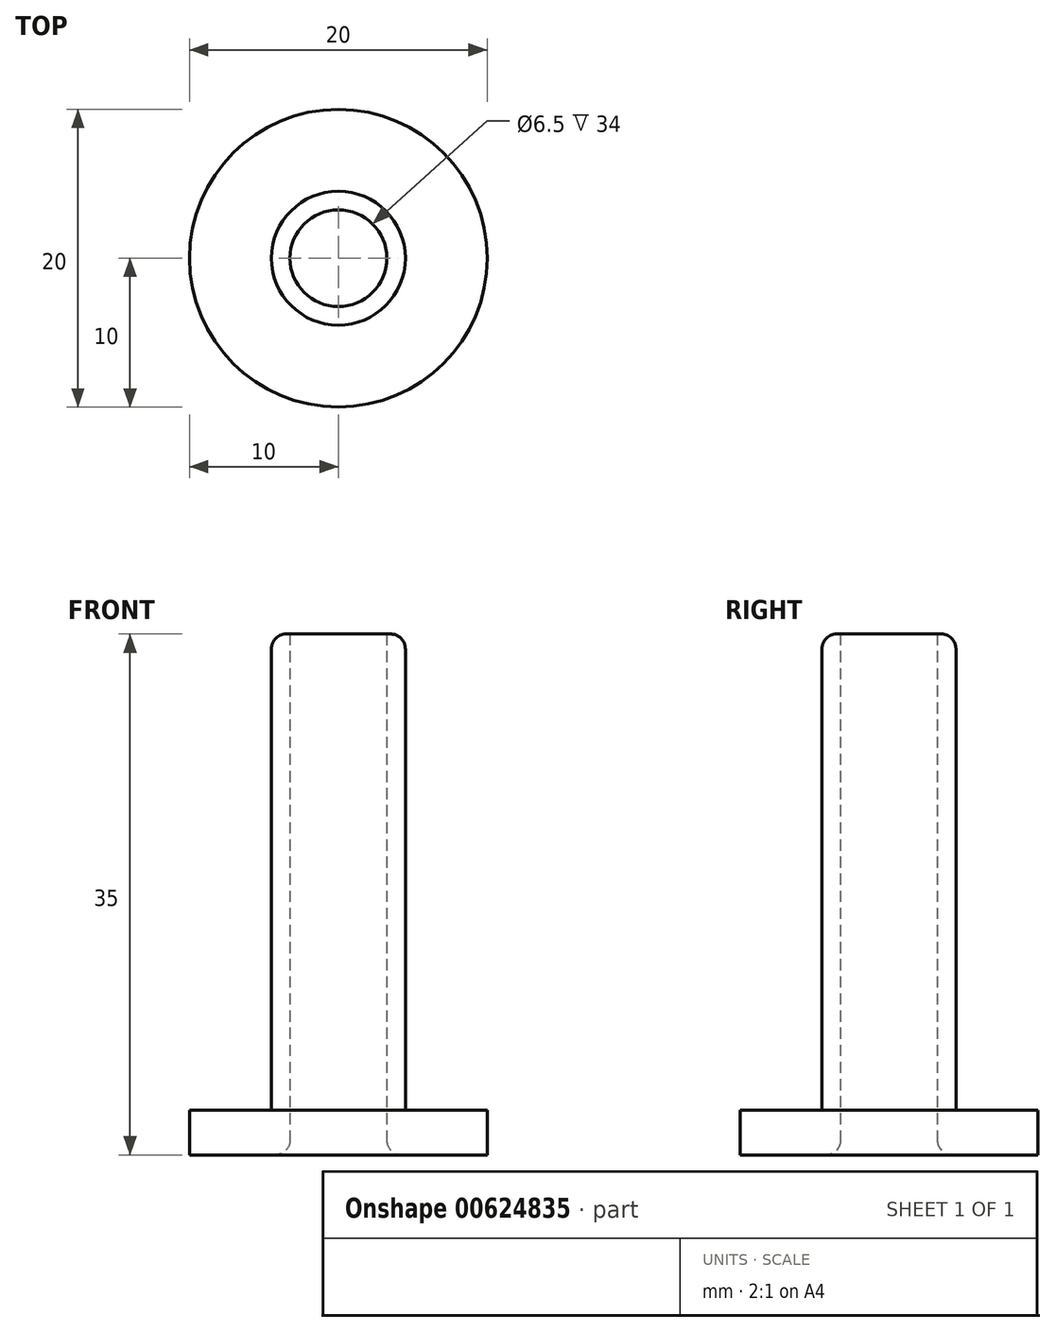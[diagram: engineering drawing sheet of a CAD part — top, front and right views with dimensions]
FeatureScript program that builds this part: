
annotation { "Feature Type Name" : "Feature", "Feature Type Description" : "" }
export const myFeature = defineFeature(function(context is Context, id is Id, definition is map)
    precondition{}
    {
        {
            var Q0;
            Q0=qCreatedBy(makeId("Top.planeOp"),FACE);
            var sketch = newSketch(context, id + "F0", { "sketchPlane" : qUnion([Q0])});
            skCircle(sketch, "E0", {"center": v(0, 0) * mm, "radius": 3.25 * mm});
            skCircle(sketch, "E1", {"center": v(0, 0) * mm, "radius": 4.5 * mm});
            skCircle(sketch, "E2", {"center": v(0, 0) * mm, "radius": 10 * mm});
            skSolve(sketch);
        }
        {
            var Q0;
            Q0 = qSketchRegion(id + "F0", true);
            var Q1;
            Q1=makeQuery(id+"F0.imprint","IMPRINT",FACE,{"disambiguationData":[TD([[makeQuery(id+"F0.imprint","IMPRINT",EDGE,{"derivedFrom":sQuery(id+"F0.wireOp",EDGE,"E0")}),-1.0]])]});
            extrude(context, id + "F1", {"entities" : qUnion([Q0, Q1]), "depth" : 3 * mm, "offsetDistance" : 25 * mm});
        }
        {
            var Q0;
            Q0=makeQuery(id+"F0.imprint","IMPRINT",FACE,{"disambiguationData":[TD([[makeQuery(id+"F0.imprint","IMPRINT",EDGE,{"derivedFrom":sQuery(id+"F0.wireOp",EDGE,"E0")}),-1.0]])]});
            extrude(context, id + "F2", {"entities" : qUnion([Q0]), "operationType" : NewBodyOperationType.ADD, "depth" : 35 * mm, "offsetDistance" : 25 * mm});
        }
        {
            var Q0;
            Q0=makeQuery(id+"F2.opExtrude","CAP_EDGE",EDGE,{"disambiguationData":[OSD([sQuery(id+"F0.wireOp",EDGE,"E1")])],"isStart":false});
            var Q1;
            Q1=makeQuery(id+"F1.opExtrude","CAP_EDGE",EDGE,{"disambiguationData":[OSD([sQuery(id+"F0.wireOp",EDGE,"E0")])],"isStart":true});
            fillet(context, id + "F3", {"entities" : qUnion([Q0, Q1]), "radius" : 1 * mm, "tangentPropagation" : true, "allowEdgeOverflow" : false});
        }
    });
